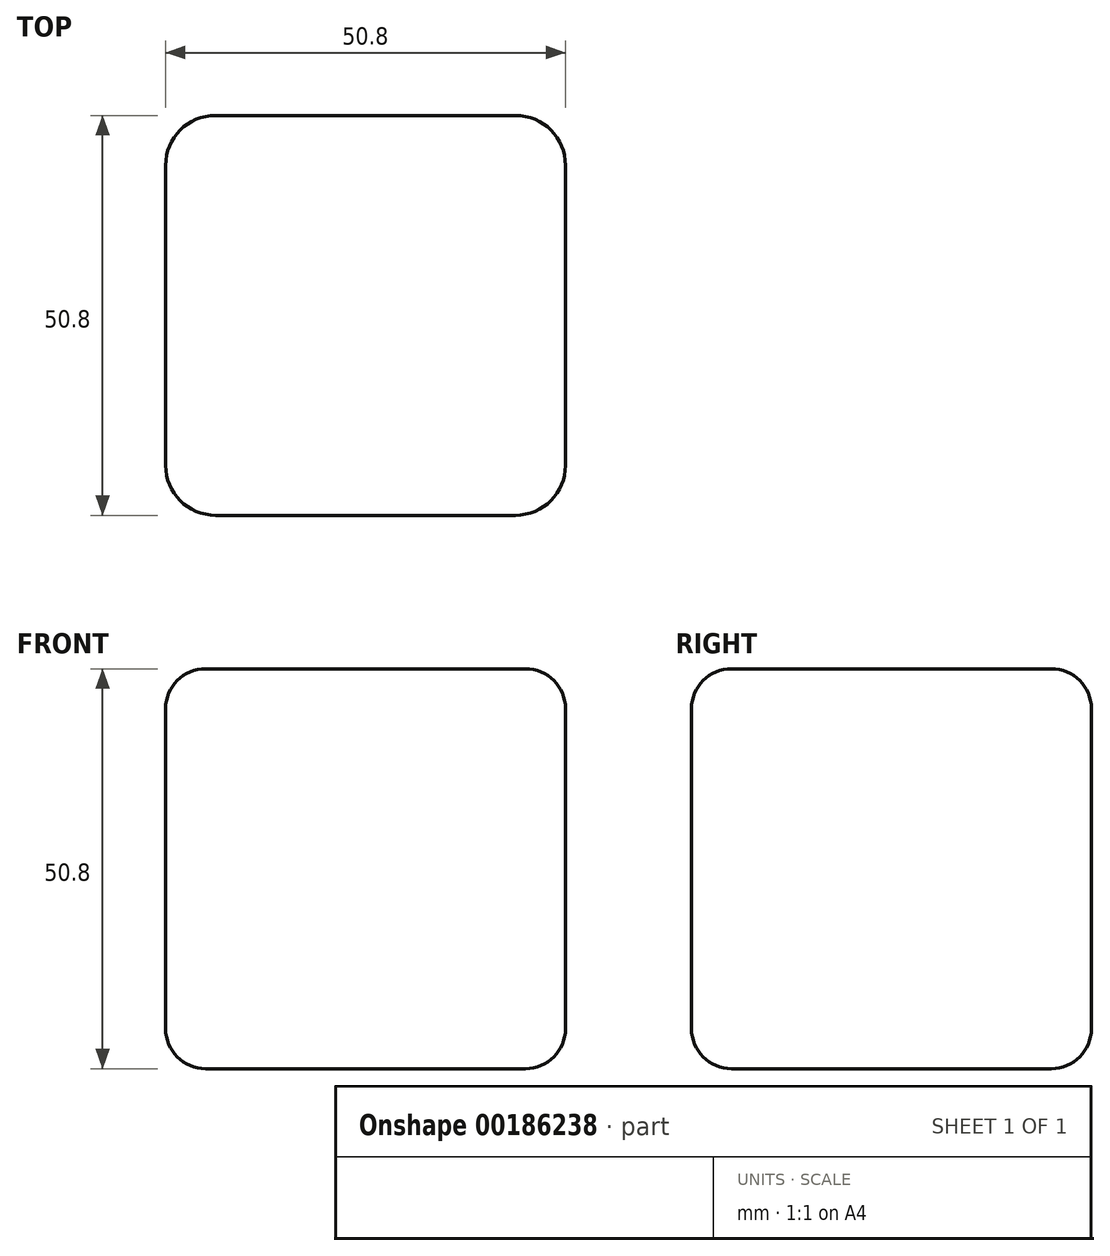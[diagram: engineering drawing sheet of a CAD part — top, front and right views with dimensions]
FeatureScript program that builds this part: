
annotation { "Feature Type Name" : "Feature", "Feature Type Description" : "" }
export const myFeature = defineFeature(function(context is Context, id is Id, definition is map)
    precondition{}
    {
        {
            var Q0;
            Q0=qCreatedBy(makeId("Top.planeOp"),FACE);
            var sketch = newSketch(context, id + "F0", { "sketchPlane" : qUnion([Q0])});
            skLineSegment(sketch, "E0.bottom", {"start": v(19.05, 25.4) * mm, "end": v(-19.05, 25.4) * mm});
            skLineSegment(sketch, "E0.top", {"start": v(19.05, -25.4) * mm, "end": v(-19.05, -25.4) * mm});
            skLineSegment(sketch, "E0.left", {"start": v(25.4, 19.05) * mm, "end": v(25.4, -19.05) * mm});
            skLineSegment(sketch, "E0.right", {"start": v(-25.4, 19.05) * mm, "end": v(-25.4, -19.05) * mm});
            skPoint(sketch, "E0.middle", {"position": v(0, 0) * mm});
            skPoint(sketch, "E1.visualSharp", {"position": v(25.4, 25.4) * mm});
            skArc(sketch, "E1.filletArc", {"start": v(25.4, 19.05) * mm, "mid": v(23.54, 23.54) * mm, "end": v(19.05, 25.4) * mm});
            skPoint(sketch, "E2.visualSharp", {"position": v(25.4, -25.4) * mm});
            skArc(sketch, "E2.filletArc", {"start": v(19.05, -25.4) * mm, "mid": v(23.54, -23.54) * mm, "end": v(25.4, -19.05) * mm});
            skPoint(sketch, "E3.visualSharp", {"position": v(-25.4, -25.4) * mm});
            skArc(sketch, "E3.filletArc", {"start": v(-25.4, -19.05) * mm, "mid": v(-23.54, -23.54) * mm, "end": v(-19.05, -25.4) * mm});
            skPoint(sketch, "E4.visualSharp", {"position": v(-25.4, 25.4) * mm});
            skArc(sketch, "E4.filletArc", {"start": v(-19.05, 25.4) * mm, "mid": v(-23.54, 23.54) * mm, "end": v(-25.4, 19.05) * mm});
            skSolve(sketch);
        }
        {
            var Q0;
            Q0=makeQuery(id+"F0.imprint","IMPRINT",FACE,{"disambiguationData":[TD([[makeQuery(id+"F0.imprint","IMPRINT",EDGE,{"derivedFrom":sQuery(id+"F0.wireOp",EDGE,"E0.bottom")}),1.0]])]});
            extrude(context, id + "F1", {"entities" : qUnion([Q0]), "depth" : 50.8 * mm});
        }
        {
            var Q0;
            Q0=makeQuery(id+"F1.opExtrude","CAP_EDGE",EDGE,{"disambiguationData":[OSD([sQuery(id+"F0.wireOp",EDGE,"E0.top")])],"isStart":false});
            fillet(context, id + "F2", {"entities" : qUnion([Q0]), "radius" : 5.08 * mm, "tangentPropagation" : true, "allowEdgeOverflow" : false});
        }
        {
            var Q0;
            Q0=makeQuery(id+"F1.opExtrude","CAP_EDGE",EDGE,{"disambiguationData":[OSD([sQuery(id+"F0.wireOp",EDGE,"E0.top")])],"isStart":true});
            fillet(context, id + "F3", {"entities" : qUnion([Q0]), "radius" : 5.08 * mm, "tangentPropagation" : true, "allowEdgeOverflow" : false});
        }
    });
